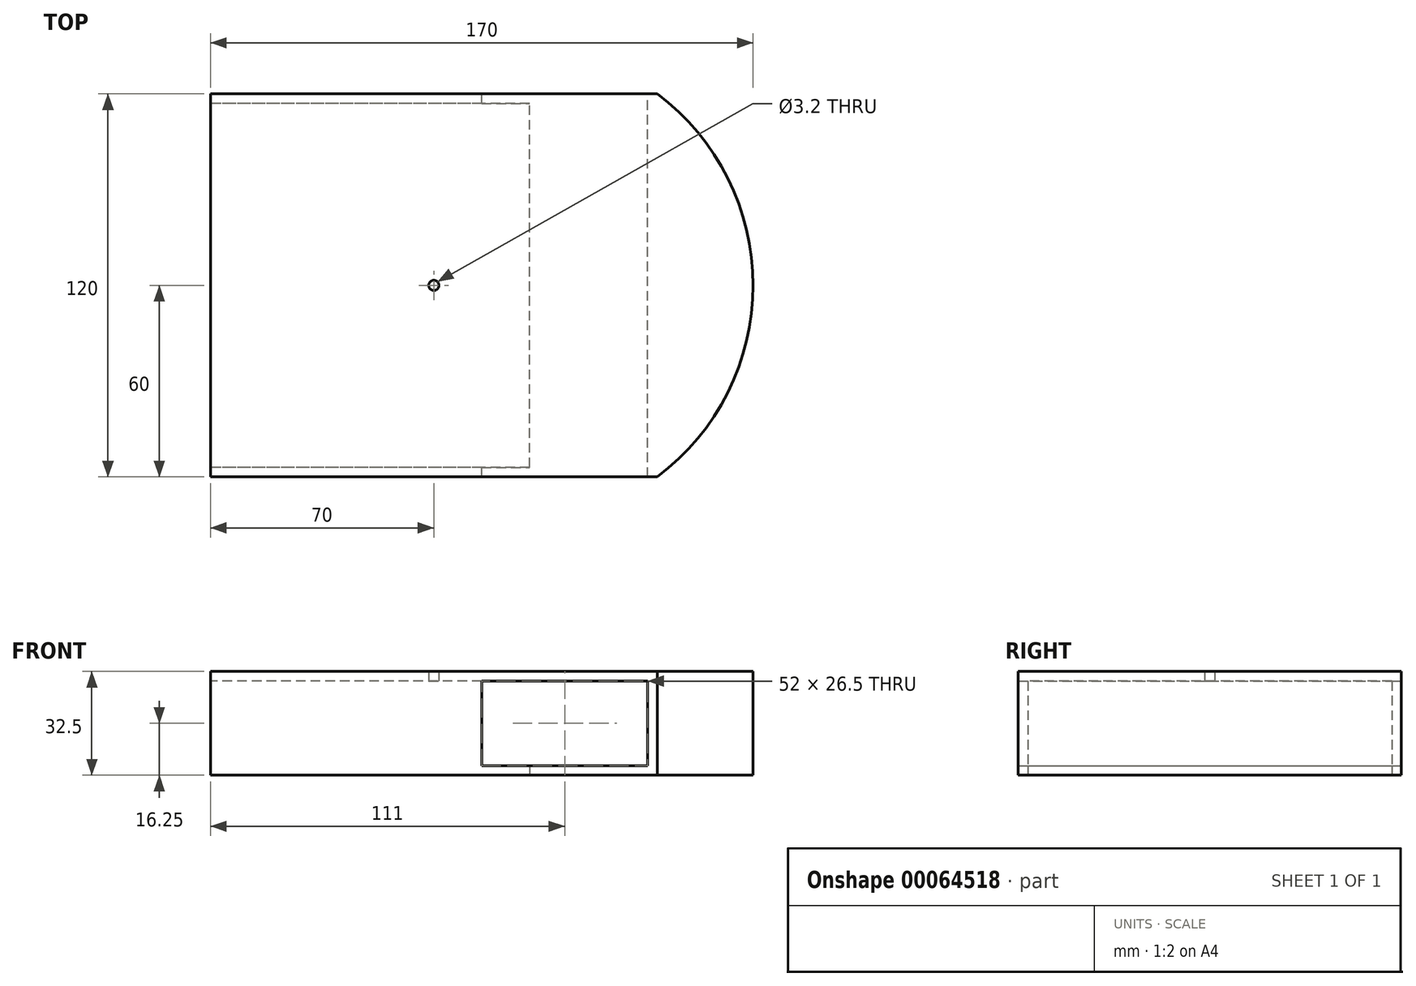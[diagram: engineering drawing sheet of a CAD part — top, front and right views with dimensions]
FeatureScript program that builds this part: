
annotation { "Feature Type Name" : "Feature", "Feature Type Description" : "" }
export const myFeature = defineFeature(function(context is Context, id is Id, definition is map)
    precondition{}
    {
        {
            var Q0;
            Q0=qCreatedBy(makeId("Top.planeOp"),FACE);
            var sketch = newSketch(context, id + "F0", { "sketchPlane" : qUnion([Q0])});
            skLineSegment(sketch, "E0.rect.bottom", {"start": v(70, -60) * mm, "end": v(-70, -60) * mm});
            skLineSegment(sketch, "E0.rect.top", {"start": v(70, 60) * mm, "end": v(-70, 60) * mm});
            skLineSegment(sketch, "E0.rect.left", {"start": v(70, -60) * mm, "end": v(70, 60) * mm});
            skLineSegment(sketch, "E0.rect.right", {"start": v(-70, -60) * mm, "end": v(-70, 60) * mm});
            skPoint(sketch, "E0.rect.middle", {"position": v(0, 0) * mm});
            skArc(sketch, "E1", {"start": v(70, -60) * mm, "mid": v(100, 0) * mm, "end": v(70, 60) * mm});
            skCircle(sketch, "E2", {"center": v(0, 0) * mm, "radius": 1.6 * mm});
            skSolve(sketch);
        }
        {
            var Q0;
            Q0=qSketchRegion(id+"F0",true);
            extrude(context, id + "F1", {"entities" : qUnion([Q0]), "depth" : 32.5 * mm});
        }
        {
            var Q0;
            Q0=makeQuery(id+"F1.opExtrude","SWEPT_FACE",FACE,{"disambiguationData":[OSD([sQuery(id+"F0.wireOp",EDGE,"E0.rect.top")])]});
            var sketch = newSketch(context, id + "F2", { "sketchPlane" : qUnion([Q0])});
            skLineSegment(sketch, "E3.bottom", {"start": v(-67, 3) * mm, "end": v(-15, 3) * mm});
            skLineSegment(sketch, "E3.top", {"start": v(-67, 29.5) * mm, "end": v(-15, 29.5) * mm});
            skLineSegment(sketch, "E3.left", {"start": v(-67, 3) * mm, "end": v(-67, 29.5) * mm});
            skLineSegment(sketch, "E3.right", {"start": v(-15, 3) * mm, "end": v(-15, 29.5) * mm});
            skSolve(sketch);
        }
        {
            var Q0;
            Q0=makeQuery(id+"F2.imprint","IMPRINT",FACE,{"disambiguationData":[TD([[makeQuery(id+"F2.imprint","IMPRINT",EDGE,{"derivedFrom":sQuery(id+"F2.wireOp",EDGE,"E3.bottom")}),1.0]])]});
            extrude(context, id + "F3", {"entities" : qUnion([Q0]), "operationType" : NewBodyOperationType.REMOVE, "oppositeDirection" : true, "depth" : 120 * mm});
        }
        {
            var Q0;
            Q0=makeQuery(id+"F1.opExtrude","SWEPT_FACE",FACE,{"disambiguationData":[OSD([sQuery(id+"F0.wireOp",EDGE,"E0.rect.right")])]});
            var sketch = newSketch(context, id + "F4", { "sketchPlane" : qUnion([Q0])});
            skLineSegment(sketch, "E4.bottom", {"start": v(-57, 29.5) * mm, "end": v(57, 29.5) * mm});
            skLineSegment(sketch, "E4.top", {"start": v(-57, 0) * mm, "end": v(57, 0) * mm});
            skLineSegment(sketch, "E4.left", {"start": v(-57, 29.5) * mm, "end": v(-57, 0) * mm});
            skLineSegment(sketch, "E4.right", {"start": v(57, 29.5) * mm, "end": v(57, 0) * mm});
            skSolve(sketch);
        }
        {
            var Q0;
            Q0=makeQuery(id+"F4.imprint","IMPRINT",FACE,{"disambiguationData":[TD([[makeQuery(id+"F4.imprint","IMPRINT",EDGE,{"derivedFrom":sQuery(id+"F4.wireOp",EDGE,"E4.bottom")}),-1.0]])]});
            extrude(context, id + "F5", {"entities" : qUnion([Q0]), "operationType" : NewBodyOperationType.REMOVE, "oppositeDirection" : true, "depth" : 100 * mm});
        }
    });
